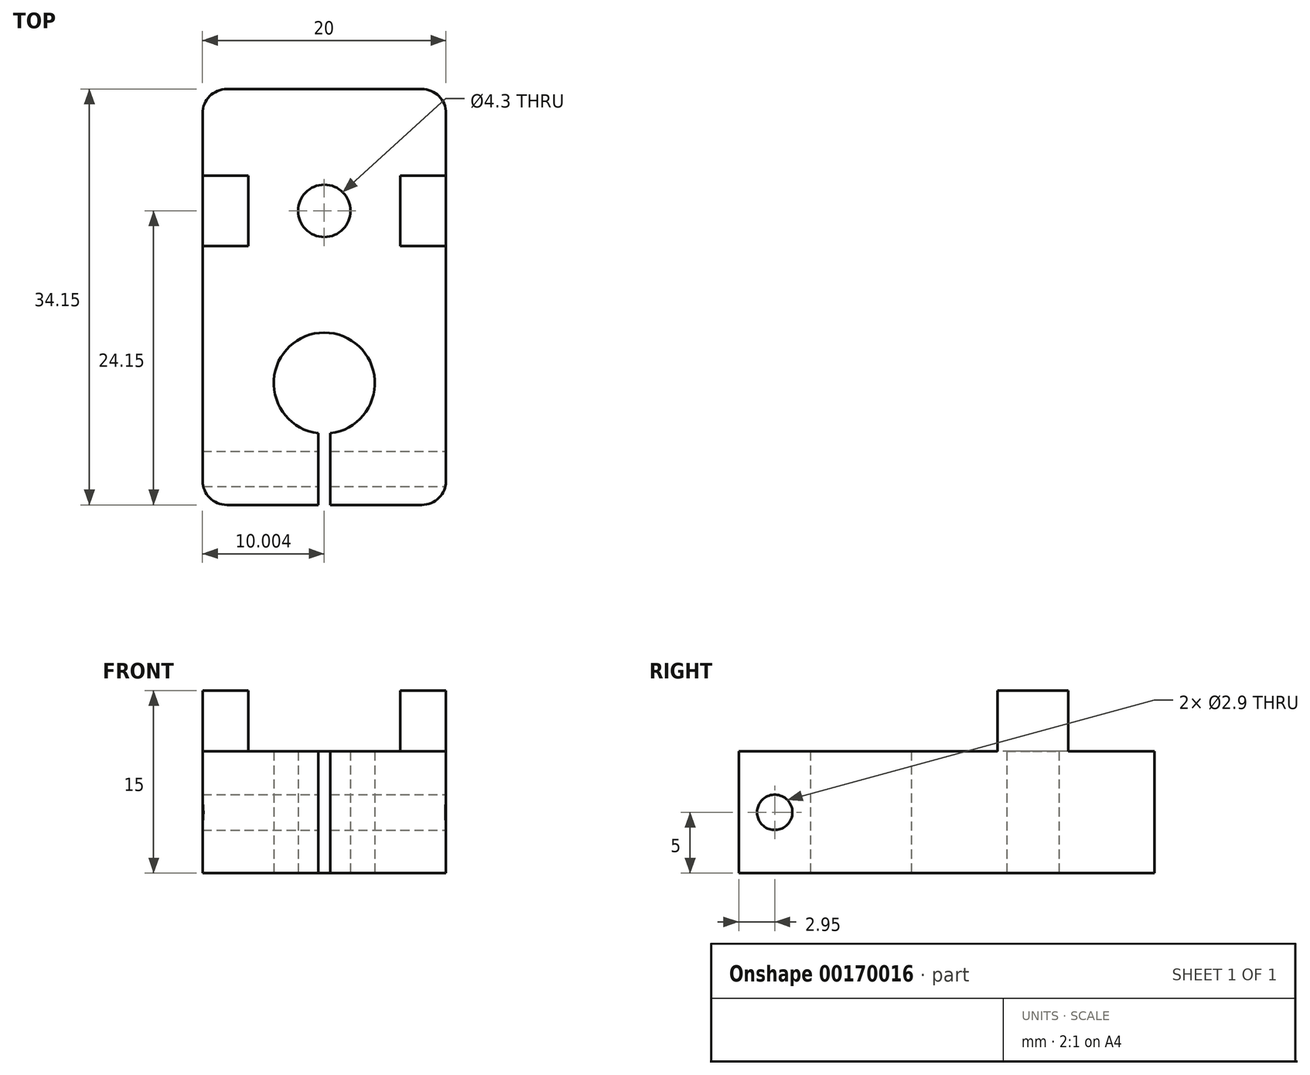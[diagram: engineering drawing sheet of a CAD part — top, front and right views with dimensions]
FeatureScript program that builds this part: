
annotation { "Feature Type Name" : "Feature", "Feature Type Description" : "" }
export const myFeature = defineFeature(function(context is Context, id is Id, definition is map)
    precondition{}
    {
        {
            var Q0;
            Q0=qCreatedBy(makeId("Top.planeOp"),FACE);
            var sketch = newSketch(context, id + "F0", { "sketchPlane" : qUnion([Q0])});
            skLineSegment(sketch, "E0.bottom", {"start": v(-7.64, 0) * mm, "end": v(12.36, 0) * mm});
            skLineSegment(sketch, "E0.top", {"start": v(-7.64, 34.15) * mm, "end": v(12.36, 34.15) * mm});
            skLineSegment(sketch, "E0.left", {"start": v(-7.64, 0) * mm, "end": v(-7.64, 34.15) * mm});
            skLineSegment(sketch, "E0.right", {"start": v(12.36, 0) * mm, "end": v(12.36, 34.15) * mm});
            skLineSegment(sketch, "E1", {"start": v(-7.64, 20) * mm, "end": v(12.36, 20) * mm, "construction": true});
            skPoint(sketch, "E2.centerSnap0", {"position": v(2.36, 34.15) * mm});
            skCircle(sketch, "E3", {"center": v(2.36, 10) * mm, "radius": 4.15 * mm});
            skLineSegment(sketch, "E4.bottom", {"start": v(2.86, 0) * mm, "end": v(1.86, 0) * mm});
            skLineSegment(sketch, "E4.top", {"start": v(2.86, 10) * mm, "end": v(1.86, 10) * mm});
            skLineSegment(sketch, "E4.left", {"start": v(2.86, 0) * mm, "end": v(2.86, 10) * mm});
            skLineSegment(sketch, "E4.right", {"start": v(1.86, 0) * mm, "end": v(1.86, 10) * mm});
            skCircle(sketch, "E5", {"center": v(2.36, 10) * mm, "radius": 7.75 * mm});
            skCircle(sketch, "E6", {"center": v(2.36, 24.15) * mm, "radius": 2.15 * mm});
            skSolve(sketch);
        }
        {
            var Q0;
            Q0=makeQuery(id+"F0.imprint","IMPRINT",FACE,{"disambiguationData":[TD([[makeQuery(id+"F0.imprint","IMPRINT",EDGE,{"derivedFrom":sQuery(id+"F0.wireOp",EDGE,"E0.top")}),-1.0]])]});
            var Q1;
            {var subQ0=sQuery(id+"F0.wireOp",EDGE,"E4.left");var subQ1=sQuery(id+"F0.wireOp",EDGE,"E3");var subQ2=makeQuery(id+"F0.imprint","INTERSECT",VERTEX,{"derivedFrom":[subQ1,subQ0]});Q1=makeQuery(id+"F0.imprint","IMPRINT",FACE,{"disambiguationData":[TD([[makeQuery(id+"F0.imprint","IMPRINT",EDGE,{"disambiguationData":[TD([[subQ2,-1.0]])],"derivedFrom":subQ1}),-1.0]])]});}
            extrude(context, id + "F1", {"entities" : qUnion([Q0, Q1]), "depth" : 10 * mm});
        }
        {
            var Q0;
            Q0=makeQuery(id+"F1.opExtrude","CAP_FACE",FACE,{"disambiguationData":[OSD([sQuery(id+"F0.wireOp",EDGE,"E0.bottom"),sQuery(id+"F0.wireOp",EDGE,"E0.top"),sQuery(id+"F0.wireOp",EDGE,"E0.left"),sQuery(id+"F0.wireOp",EDGE,"E0.right"),sQuery(id+"F0.wireOp",EDGE,"E2")])],"isStart":false});
            var sketch = newSketch(context, id + "F2", { "sketchPlane" : qUnion([Q0])});
            skLineSegment(sketch, "E7.bottom", {"start": v(-7.64, 27.05) * mm, "end": v(-3.89, 27.05) * mm});
            skLineSegment(sketch, "E7.top", {"start": v(-7.64, 21.25) * mm, "end": v(-3.89, 21.25) * mm});
            skLineSegment(sketch, "E7.left", {"start": v(-7.64, 27.05) * mm, "end": v(-7.64, 21.25) * mm});
            skLineSegment(sketch, "E7.right", {"start": v(-3.89, 27.05) * mm, "end": v(-3.89, 21.25) * mm});
            skLineSegment(sketch, "E8.bottom", {"start": v(12.36, 27.05) * mm, "end": v(8.61, 27.05) * mm});
            skLineSegment(sketch, "E8.top", {"start": v(12.36, 21.25) * mm, "end": v(8.61, 21.25) * mm});
            skLineSegment(sketch, "E8.left", {"start": v(12.36, 27.05) * mm, "end": v(12.36, 21.25) * mm});
            skLineSegment(sketch, "E8.right", {"start": v(8.61, 27.05) * mm, "end": v(8.61, 21.25) * mm});
            skPoint(sketch, "E9", {"position": v(-3.89, 24.15) * mm});
            skPoint(sketch, "E10", {"position": v(2.36, 24.15) * mm});
            skSolve(sketch);
        }
        {
            var Q0;
            Q0=qSketchRegion(id+"F2",true);
            extrude(context, id + "F3", {"entities" : qUnion([Q0]), "operationType" : NewBodyOperationType.ADD, "depth" : 5 * mm});
        }
        {
            var Q0;
            Q0=makeQuery(id+"F3.boolean.opBoolean","MERGE",FACE,{"derivedFrom":[makeQuery(id+"F1.opExtrude","SWEPT_FACE",FACE,{"disambiguationData":[OSD([sQuery(id+"F0.wireOp",EDGE,"E0.right")])]}),makeQuery(id+"F3.opExtrude","SWEPT_FACE",FACE,{"disambiguationData":[OSD([sQuery(id+"F2.wireOp",EDGE,"E8.left")])]})]});
            var sketch = newSketch(context, id + "F4", { "sketchPlane" : qUnion([Q0])});
            skCircle(sketch, "E11", {"center": v(2.95, 5) * mm, "radius": 1.45 * mm});
            skPoint(sketch, "E11.centerSnap0", {"position": v(0, 5) * mm});
            skSolve(sketch);
        }
        {
            var Q0;
            Q0=qSketchRegion(id+"F4",true);
            extrude(context, id + "F5", {"entities" : qUnion([Q0]), "operationType" : NewBodyOperationType.REMOVE, "oppositeDirection" : true, "depth" : 25 * mm});
        }
        {
            var Q0;
            Q0=makeQuery(id+"F1.opExtrude","SWEPT_EDGE",EDGE,{"disambiguationData":[OSD([sQuery(id+"F0.wireOp",EDGE,"E0.bottom"),sQuery(id+"F0.wireOp",EDGE,"E0.right")])]});
            var Q1;
            Q1=makeQuery(id+"F1.opExtrude","SWEPT_EDGE",EDGE,{"disambiguationData":[OSD([sQuery(id+"F0.wireOp",EDGE,"E0.bottom"),sQuery(id+"F0.wireOp",EDGE,"E0.left")])]});
            var Q2;
            Q2=makeQuery(id+"F1.opExtrude","SWEPT_EDGE",EDGE,{"disambiguationData":[OSD([sQuery(id+"F0.wireOp",EDGE,"E0.top"),sQuery(id+"F0.wireOp",EDGE,"E0.right")])]});
            var Q3;
            Q3=makeQuery(id+"F1.opExtrude","SWEPT_EDGE",EDGE,{"disambiguationData":[OSD([sQuery(id+"F0.wireOp",EDGE,"E0.top"),sQuery(id+"F0.wireOp",EDGE,"E0.left")])]});
            fillet(context, id + "F6", {"entities" : qUnion([Q0, Q1, Q2, Q3]), "radius" : 2 * mm, "tangentPropagation" : true, "allowEdgeOverflow" : false});
        }
    });
